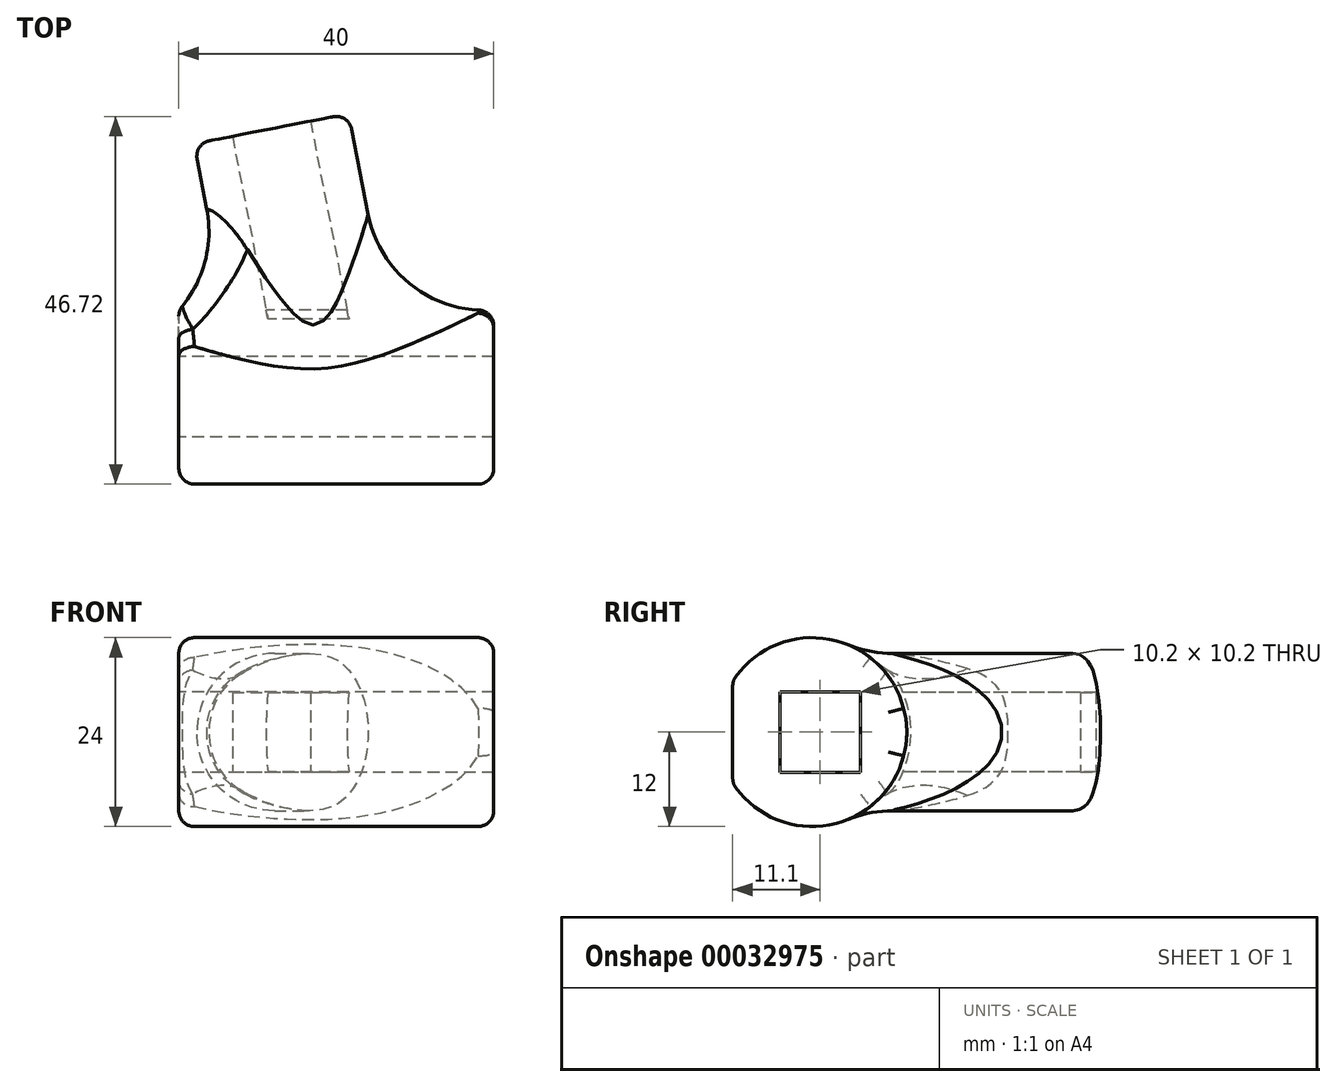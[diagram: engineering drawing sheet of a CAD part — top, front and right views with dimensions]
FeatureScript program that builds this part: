
annotation { "Feature Type Name" : "Feature", "Feature Type Description" : "" }
export const myFeature = defineFeature(function(context is Context, id is Id, definition is map)
    precondition{}
    {
        {
            var Q0;
            Q0=qCreatedBy(makeId("Right.planeOp"),FACE);
            var sketch = newSketch(context, id + "F0", { "sketchPlane" : qUnion([Q0])});
            skArc(sketch, "E0", {"start": v(-11.1, -6.48) * mm, "mid": v(11, 0) * mm, "end": v(-11.1, 6.48) * mm});
            skLineSegment(sketch, "E1.rect.bottom", {"start": v(5.1, -5.1) * mm, "end": v(-5.1, -5.1) * mm});
            skLineSegment(sketch, "E1.rect.top", {"start": v(5.1, 5.1) * mm, "end": v(-5.1, 5.1) * mm});
            skLineSegment(sketch, "E1.rect.left", {"start": v(5.1, -5.1) * mm, "end": v(5.1, 5.1) * mm});
            skLineSegment(sketch, "E1.rect.right", {"start": v(-5.1, -5.1) * mm, "end": v(-5.1, 5.1) * mm});
            skPoint(sketch, "E1.rect.middle", {"position": v(0, 0) * mm});
            skLineSegment(sketch, "E2", {"start": v(-11.1, 6.48) * mm, "end": v(-11.1, -6.48) * mm});
            skSolve(sketch);
        }
        {
            var Q0;
            Q0 = qSketchRegion(id + "F0", true);
            extrude(context, id + "F1", {"entities" : qUnion([Q0]), "depth" : 40 * mm});
        }
        {
            var Q0;
            Q0=qCreatedBy(makeId("Front.planeOp"),FACE);
            var sketch = newSketch(context, id + "F2", { "sketchPlane" : qUnion([Q0])});
            skLineSegment(sketch, "E3", {"start": v(20, 23.36) * mm, "end": v(20, -30.04) * mm, "construction": true});
            skSolve(sketch);
        }
        {
            var Q0;
            Q0=sQuery(id+"F2.wireOp",EDGE,"E3");
            cPlane(context, id + "F3", {"entities" : qUnion([Q0]), "cplaneType" : CPlaneType.LINE_ANGLE, "offset" : 150 * mm, "angle" : 79 * degree, "width" : 150 * mm, "height" : 150 * mm});
        }
        {
            var Q0;
            Q0=qCreatedBy(id+"F3.planeOp",FACE);
            var sketch = newSketch(context, id + "F4", { "sketchPlane" : qUnion([Q0])});
            skCircle(sketch, "E4", {"center": v(-18.04, 0) * mm, "radius": 10 * mm});
            skLineSegment(sketch, "E5.rect.bottom", {"start": v(-13, 5.05) * mm, "end": v(-23.1, 5.05) * mm});
            skLineSegment(sketch, "E5.rect.top", {"start": v(-13, -5.05) * mm, "end": v(-23.1, -5.05) * mm});
            skLineSegment(sketch, "E5.rect.left", {"start": v(-13, 5.05) * mm, "end": v(-13, -5.05) * mm});
            skLineSegment(sketch, "E5.rect.right", {"start": v(-23.1, 5.05) * mm, "end": v(-23.1, -5.05) * mm});
            skSolve(sketch);
        }
        {
            var Q0;
            Q0 = qSketchRegion(id + "F4", true);
            extrude(context, id + "F5", {"entities" : qUnion([Q0]), "operationType" : NewBodyOperationType.ADD, "depth" : 35 * mm});
        }
        {
            var Q0;
            Q0=makeQuery(id+"F5.boolean.opBoolean","INTERSECT",EDGE,{"disambiguationData":[OD(4.0)],"derivedFrom":[makeQuery(id+"F1.opExtrude","SWEPT_FACE",FACE,{"disambiguationData":[OSD([sQuery(id+"F0.wireOp",EDGE,"E0")])]}),makeQuery(id+"F5.opExtrude","SWEPT_FACE",FACE,{"disambiguationData":[OSD([sQuery(id+"F4.wireOp",EDGE,"E4")])]})]});
            fillet(context, id + "F6", {"entities" : qUnion([Q0]), "radius" : 15 * mm, "tangentPropagation" : true, "allowEdgeOverflow" : false});
        }
        {
            var Q0;
            Q0=makeQuery(id+"F1.opExtrude","CAP_FACE",FACE,{"disambiguationData":[OSD([sQuery(id+"F0.wireOp",EDGE,"E0"),sQuery(id+"F0.wireOp",EDGE,"E1.rect.bottom"),sQuery(id+"F0.wireOp",EDGE,"E1.rect.top"),sQuery(id+"F0.wireOp",EDGE,"E1.rect.left"),sQuery(id+"F0.wireOp",EDGE,"E1.rect.right")])],"isStart":false});
            var sketch = newSketch(context, id + "F7", { "sketchPlane" : qUnion([Q0])});
            skLineSegment(sketch, "E6.rect.bottom", {"start": v(-5.1, -5.1) * mm, "end": v(5.1, -5.1) * mm});
            skLineSegment(sketch, "E6.rect.top", {"start": v(-5.1, 5.1) * mm, "end": v(5.1, 5.1) * mm});
            skLineSegment(sketch, "E6.rect.left", {"start": v(-5.1, -5.1) * mm, "end": v(-5.1, 5.1) * mm});
            skLineSegment(sketch, "E6.rect.right", {"start": v(5.1, -5.1) * mm, "end": v(5.1, 5.1) * mm});
            skPoint(sketch, "E6.rect.middle", {"position": v(-1, 0) * mm});
            skSolve(sketch);
        }
        {
            var Q0;
            Q0 = qSketchRegion(id + "F7", true);
            extrude(context, id + "F8", {"entities" : qUnion([Q0]), "operationType" : NewBodyOperationType.REMOVE, "endBound" : BoundingType.THROUGH_ALL, "oppositeDirection" : true, "depth" : 25 * mm});
        }
        {
            var Q0;
            Q0=makeQuery(id+"F5.opExtrude","CAP_EDGE",EDGE,{"disambiguationData":[OSD([sQuery(id+"F4.wireOp",EDGE,"E4")])],"isStart":false});
            var Q1;
            Q1=makeQuery(id+"F1.opExtrude","CAP_EDGE",EDGE,{"disambiguationData":[OSD([sQuery(id+"F0.wireOp",EDGE,"E0")])],"isStart":true});
            var Q2;
            Q2=makeQuery(id+"F1.opExtrude","CAP_EDGE",EDGE,{"disambiguationData":[OSD([sQuery(id+"F0.wireOp",EDGE,"E0")])],"isStart":false});
            var Q3;
            Q3=makeQuery(id+"F1.opExtrude","SWEPT_FACE",FACE,{"disambiguationData":[OSD([sQuery(id+"F0.wireOp",EDGE,"E2")])]});
            fillet(context, id + "F9", {"entities" : qUnion([Q0, Q1, Q2, Q3]), "radius" : 2 * mm, "tangentPropagation" : true, "allowEdgeOverflow" : false});
        }
    });
